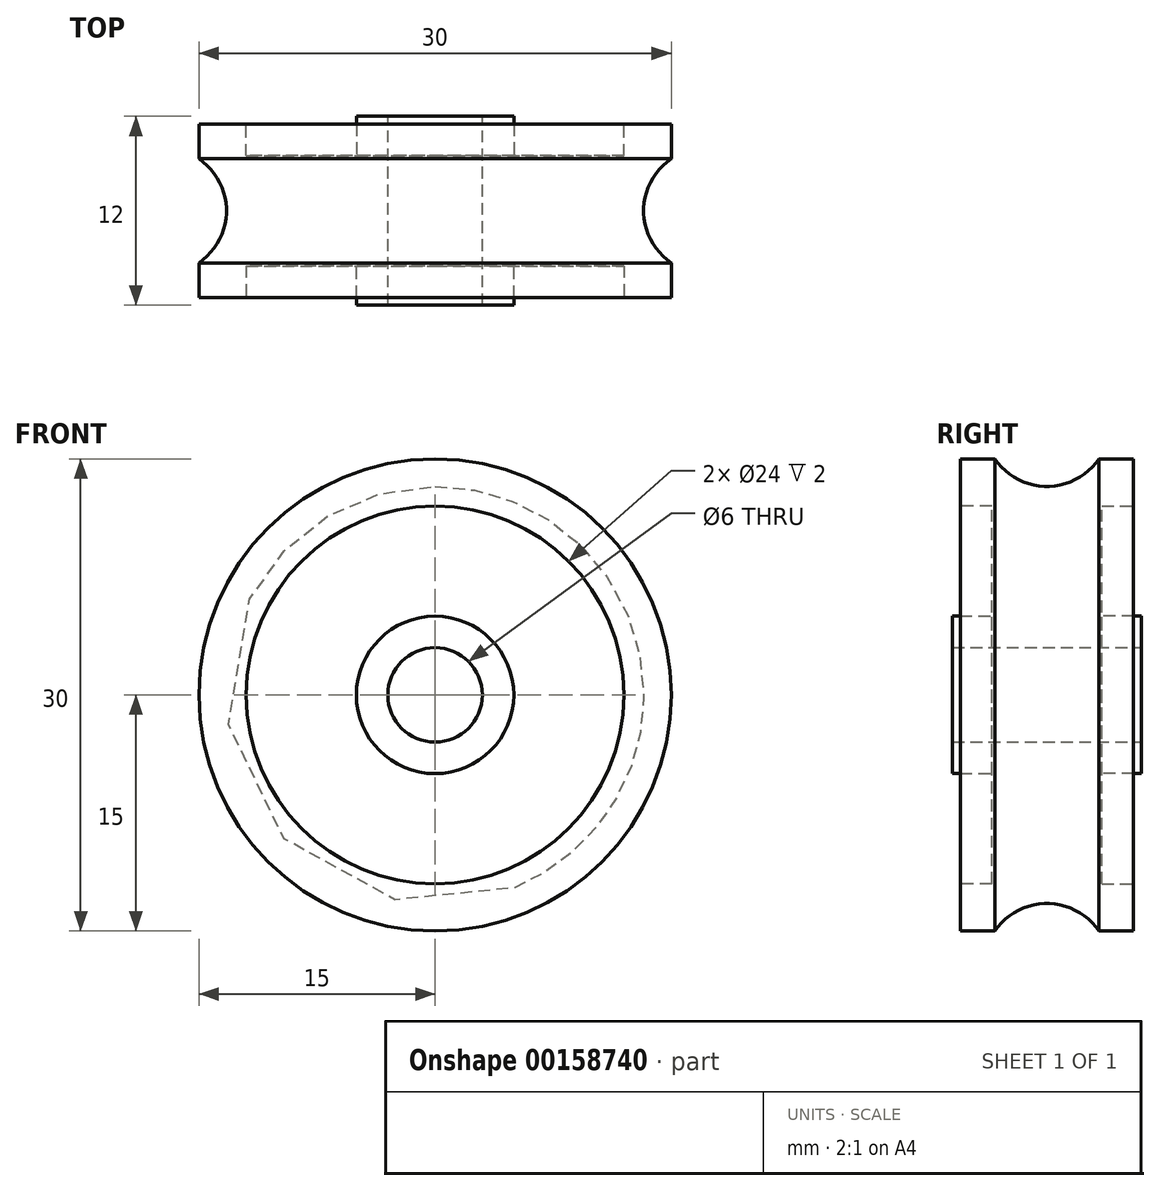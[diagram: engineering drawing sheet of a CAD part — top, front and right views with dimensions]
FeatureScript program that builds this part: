
annotation { "Feature Type Name" : "Feature", "Feature Type Description" : "" }
export const myFeature = defineFeature(function(context is Context, id is Id, definition is map)
    precondition{}
    {
        {
            var Q0;
            Q0=qCreatedBy(makeId("Top.planeOp"),FACE);
            var sketch = newSketch(context, id + "F0", { "sketchPlane" : qUnion([Q0])});
            skLineSegment(sketch, "E0", {"start": v(0, 0) * mm, "end": v(-13.25, 0) * mm});
            skPoint(sketch, "E1", {"position": v(-13.25, 0) * mm});
            skArc(sketch, "E2", {"start": v(-15, -3.3) * mm, "mid": v(-13.71, -1.87) * mm, "end": v(-13.25, 0) * mm});
            skLineSegment(sketch, "E3.top", {"start": v(-15, -5.5) * mm, "end": v(0, -5.5) * mm});
            skPoint(sketch, "E3.middle", {"position": v(0, 0) * mm});
            skLineSegment(sketch, "E4", {"start": v(0, 0) * mm, "end": v(0, -5.5) * mm});
            skPoint(sketch, "E3.right.end.orphan", {"position": v(15, -5.5) * mm});
            skPoint(sketch, "E3.right.start.orphan", {"position": v(15, 5.5) * mm});
            skLineSegment(sketch, "E5.trimOffspring", {"start": v(-15, -3.3) * mm, "end": v(-15, -5.5) * mm});
            skSolve(sketch);
        }
        {
            var Q0;
            {var subQ1=sQuery(id+"F0.wireOp",EDGE,"E0");Q0=makeQuery(id+"F0.imprint","IMPRINT",FACE,{"disambiguationData":[TD([[makeQuery(id+"F0.imprint","IMPRINT",EDGE,{"derivedFrom":subQ1}),1.0]])]});}
            var Q1;
            Q1=sQuery(id+"F0.wireOp",EDGE,"E4");
            revolve(context, id + "F1", {"entities" : qUnion([Q0]), "axis" : qUnion([Q1]), "revolveType" : RevolveType.FULL});
        }
        {
            var Q0;
            Q0=makeQuery(id+"F1.opRevolve","SWEPT_FACE",FACE,{"disambiguationData":[OSD([sQuery(id+"F0.wireOp",EDGE,"E3.top")])]});
            var sketch = newSketch(context, id + "F2", { "sketchPlane" : qUnion([Q0])});
            skCircle(sketch, "E6", {"center": v(0, 0) * mm, "radius": 5 * mm});
            skCircle(sketch, "E7", {"center": v(0, 0) * mm, "radius": 3 * mm});
            skCircle(sketch, "E8", {"center": v(0, 0) * mm, "radius": 12 * mm});
            skSolve(sketch);
        }
        {
            var Q0;
            Q0=makeQuery(id+"F2.imprint","IMPRINT",FACE,{"disambiguationData":[TD([[makeQuery(id+"F2.imprint","IMPRINT",EDGE,{"derivedFrom":sQuery(id+"F2.wireOp",EDGE,"E6")}),1.0]])]});
            extrude(context, id + "F3", {"entities" : qUnion([Q0]), "operationType" : NewBodyOperationType.ADD, "depth" : 0.5 * mm});
        }
        {
            var Q0;
            Q0=makeQuery(id+"F2.imprint","IMPRINT",FACE,{"disambiguationData":[TD([[makeQuery(id+"F2.imprint","IMPRINT",EDGE,{"derivedFrom":sQuery(id+"F2.wireOp",EDGE,"E6")}),-1.0]])]});
            extrude(context, id + "F4", {"entities" : qUnion([Q0]), "operationType" : NewBodyOperationType.REMOVE, "oppositeDirection" : true, "depth" : 2 * mm});
        }
        {
            var Q0;
            Q0=makeQuery(id+"F3.boolean.opBoolean","SPLIT",FACE,{"disambiguationData":[TD([makeQuery(id+"F3.opExtrude","SWEPT_FACE",FACE,{"disambiguationData":[OSD([sQuery(id+"F2.wireOp",EDGE,"E7")])]})])],"derivedFrom":makeQuery(id+"F1.opRevolve","SWEPT_FACE",FACE,{"disambiguationData":[OSD([sQuery(id+"F0.wireOp",EDGE,"E3.top")])]})});
            extrude(context, id + "F5", {"entities" : qUnion([Q0]), "operationType" : NewBodyOperationType.REMOVE, "oppositeDirection" : true, "depth" : 25 * mm});
        }
        {
            var Q0;
            Q0=makeQuery(id+"F1.opRevolve","SWEPT_BODY",BODY,{"disambiguationData":[OSD([sQuery(id+"F0.wireOp",EDGE,"E2"),sQuery(id+"F0.wireOp",EDGE,"E3.bottom"),sQuery(id+"F0.wireOp",EDGE,"E3.top"),sQuery(id+"F0.wireOp",EDGE,"E3.left"),sQuery(id+"F0.wireOp",EDGE,"Q0bHfnxd-mlwY-3Qlx-kkkn-em1jF3xmF4ry"),sQuery(id+"F0.wireOp",EDGE,"E4")])]});
            var Q1;
            Q1=qCreatedBy(makeId("Front.planeOp"),FACE);
            mirror(context, id + "F6", {"operationType" : NewBodyOperationType.ADD, "entities" : qUnion([Q0]), "mirrorPlane" : qUnion([Q1])});
        }
    });
